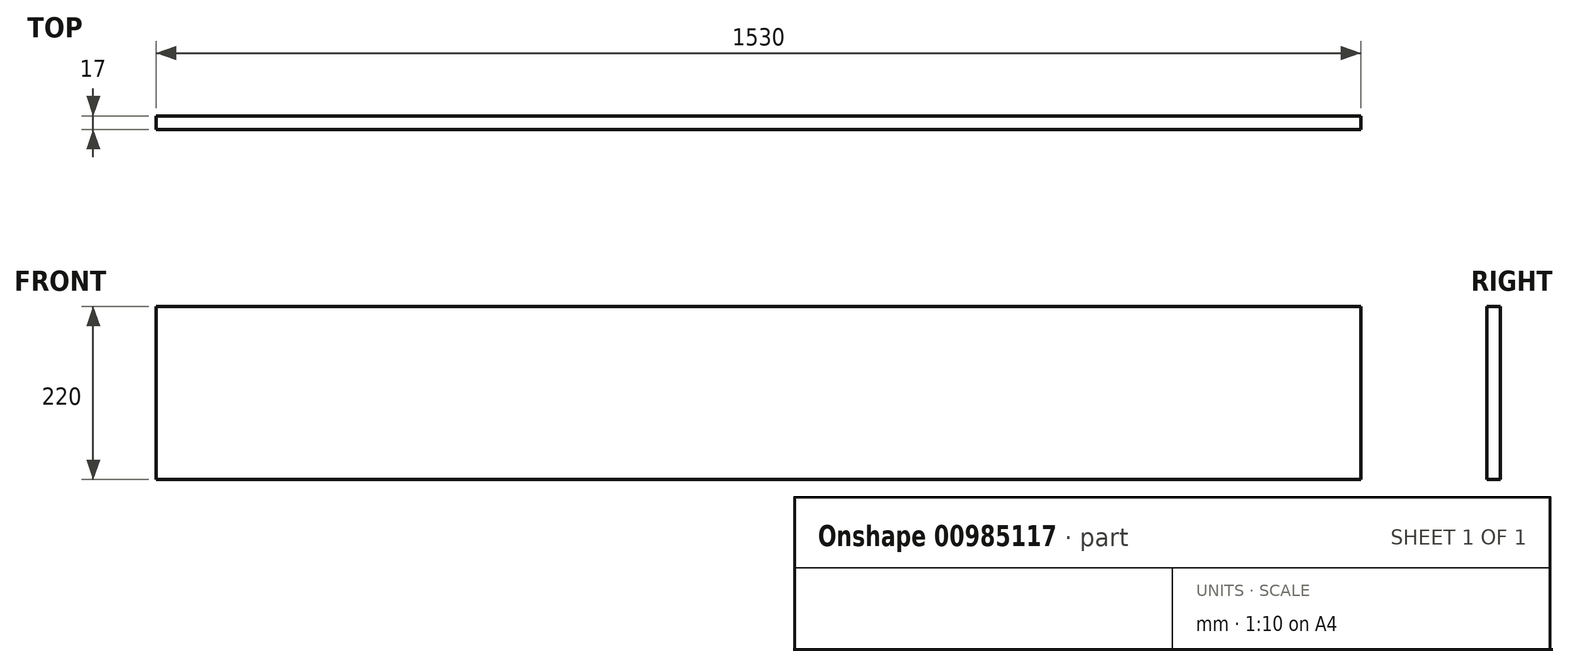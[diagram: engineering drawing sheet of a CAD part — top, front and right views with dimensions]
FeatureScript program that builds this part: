
annotation { "Feature Type Name" : "Feature", "Feature Type Description" : "" }
export const myFeature = defineFeature(function(context is Context, id is Id, definition is map)
    precondition{}
    {
        {
            var Q0;
            Q0=qCreatedBy(makeId("Front.planeOp"),FACE);
            var sketch = newSketch(context, id + "F0", { "sketchPlane" : qUnion([Q0])});
            skLineSegment(sketch, "E0.bottom", {"start": v(-83.08, 195.83) * mm, "end": v(1446.92, 195.83) * mm});
            skLineSegment(sketch, "E0.top", {"start": v(-83.08, -24.17) * mm, "end": v(1446.92, -24.17) * mm});
            skLineSegment(sketch, "E0.left", {"start": v(-83.08, 195.83) * mm, "end": v(-83.08, -24.17) * mm});
            skLineSegment(sketch, "E0.right", {"start": v(1446.92, 195.83) * mm, "end": v(1446.92, -24.17) * mm});
            skSolve(sketch);
        }
        {
            var Q0;
            Q0 = qSketchRegion(id + "F0", true);
            extrude(context, id + "F1", {"entities" : qUnion([Q0]), "depth" : 17 * mm, "offsetDistance" : 25 * mm});
        }
    });
